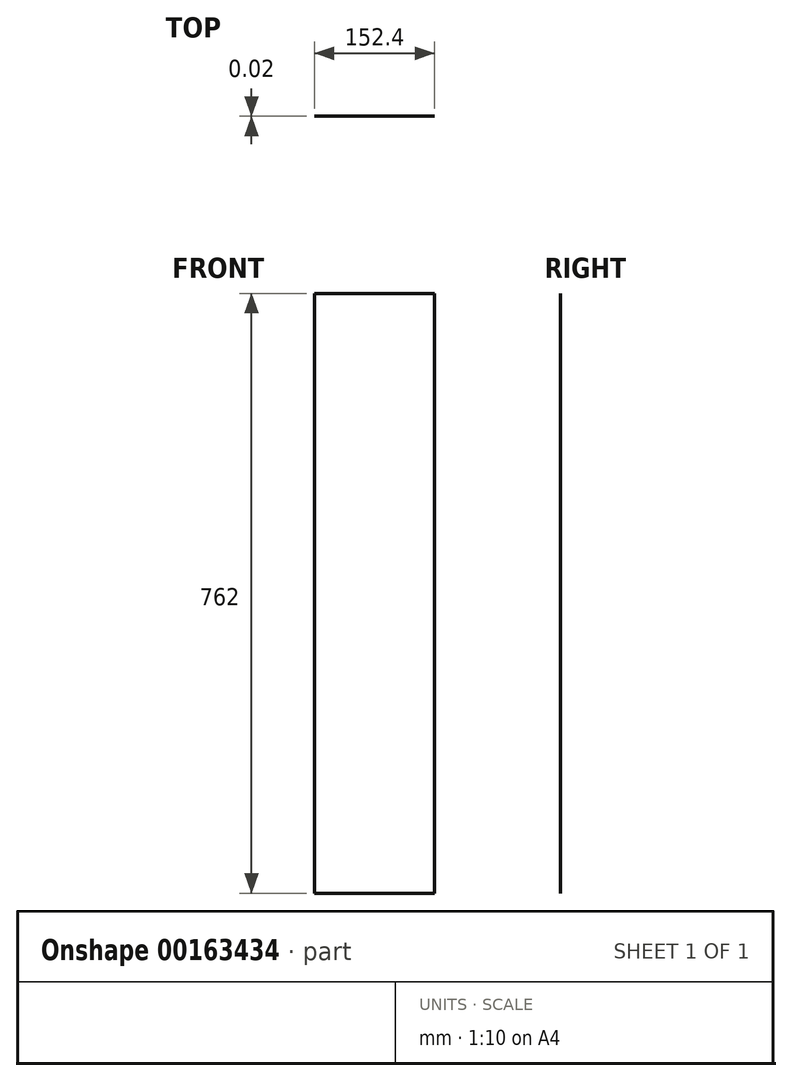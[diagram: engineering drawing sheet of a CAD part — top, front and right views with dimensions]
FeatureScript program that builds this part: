
annotation { "Feature Type Name" : "Feature", "Feature Type Description" : "" }
export const myFeature = defineFeature(function(context is Context, id is Id, definition is map)
    precondition{}
    {
        {
            var Q0;
            Q0=qCreatedBy(makeId("Front.planeOp"),FACE);
            var sketch = newSketch(context, id + "F0", { "sketchPlane" : qUnion([Q0])});
            skLineSegment(sketch, "E0.bottom", {"start": v(0, 0) * mm, "end": v(152.4, 0) * mm});
            skLineSegment(sketch, "E0.top", {"start": v(0, 762) * mm, "end": v(152.4, 762) * mm});
            skLineSegment(sketch, "E0.left", {"start": v(0, 0) * mm, "end": v(0, 762) * mm});
            skLineSegment(sketch, "E0.right", {"start": v(152.4, 0) * mm, "end": v(152.4, 762) * mm});
            skSolve(sketch);
        }
        {
            var Q0;
            Q0=makeQuery(id+"F0.imprint","IMPRINT",FACE,{"disambiguationData":[TD([[makeQuery(id+"F0.imprint","IMPRINT",EDGE,{"derivedFrom":sQuery(id+"F0.wireOp",EDGE,"E0.bottom")}),1.0]])]});
            extrude(context, id + "F1", {"entities" : qUnion([Q0]), "depth" : 5 / 203.2 * mm});
        }
    });
